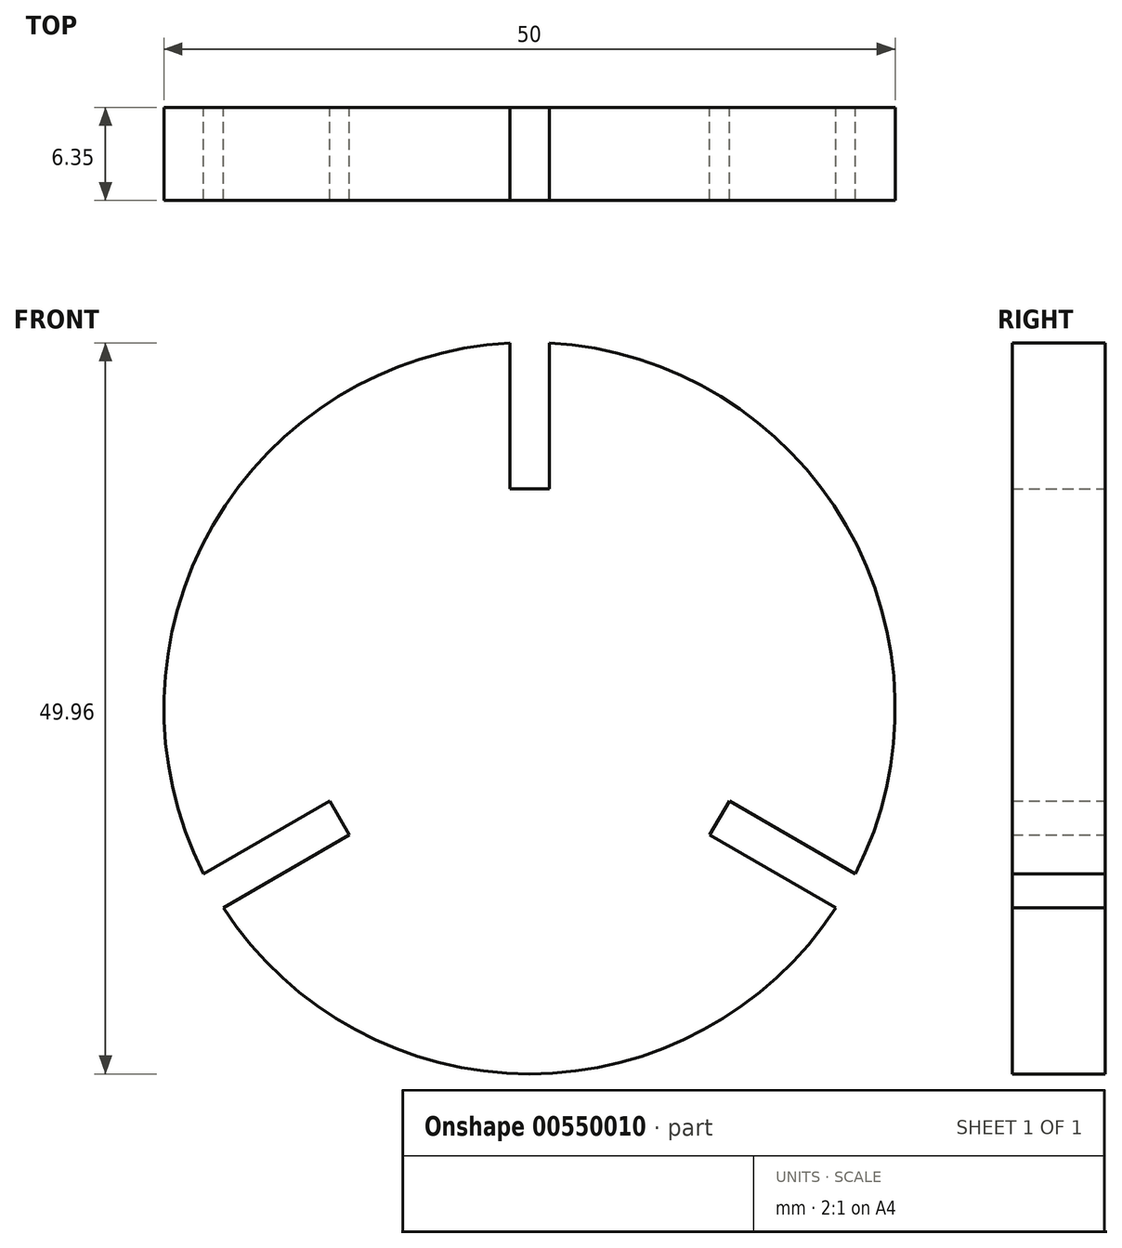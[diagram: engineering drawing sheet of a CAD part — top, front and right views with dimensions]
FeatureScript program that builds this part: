
annotation { "Feature Type Name" : "Feature", "Feature Type Description" : "" }
export const myFeature = defineFeature(function(context is Context, id is Id, definition is map)
    precondition{}
    {
        {
            var Q0;
            Q0=qCreatedBy(makeId("Front.planeOp"),FACE);
            var sketch = newSketch(context, id + "F0", { "sketchPlane" : qUnion([Q0])});
            skArc(sketch, "E0", {"start": v(-1.35, 24.96) * mm, "mid": v(-21.65, 12.5) * mm, "end": v(-22.3, -11.31) * mm});
            skLineSegment(sketch, "E1.bottom", {"start": v(-1.35, 15) * mm, "end": v(1.35, 15) * mm});
            skLineSegment(sketch, "E1.left", {"start": v(-1.35, 15) * mm, "end": v(-1.35, 24.96) * mm});
            skLineSegment(sketch, "E1.right", {"start": v(1.35, 15) * mm, "end": v(1.35, 24.96) * mm});
            skPoint(sketch, "E1.middle", {"position": v(0, 25) * mm});
            skPoint(sketch, "E1.top.end.orphan", {"position": v(1.35, 35) * mm});
            skPoint(sketch, "E1.top.start.orphan", {"position": v(-1.35, 35) * mm});
            skLineSegment(sketch, "E2.1.0", {"start": v(-13.67, -6.33) * mm, "end": v(-22.3, -11.31) * mm});
            skLineSegment(sketch, "E2.1.1", {"start": v(-12.32, -8.67) * mm, "end": v(-20.94, -13.65) * mm});
            skLineSegment(sketch, "E2.1.2", {"start": v(-12.32, -8.67) * mm, "end": v(-13.67, -6.33) * mm});
            skLineSegment(sketch, "E2.2.0", {"start": v(12.32, -8.67) * mm, "end": v(20.94, -13.65) * mm});
            skLineSegment(sketch, "E2.2.1", {"start": v(13.67, -6.33) * mm, "end": v(22.3, -11.31) * mm});
            skLineSegment(sketch, "E2.2.2", {"start": v(13.67, -6.33) * mm, "end": v(12.32, -8.67) * mm});
            skArc(sketch, "E3.trimOffspring", {"start": v(-20.94, -13.65) * mm, "mid": v(0, -25) * mm, "end": v(20.94, -13.65) * mm});
            skArc(sketch, "E4.trimOffspring", {"start": v(22.3, -11.31) * mm, "mid": v(21.65, 12.5) * mm, "end": v(1.35, 24.96) * mm});
            skSolve(sketch);
        }
        {
            var Q0;
            Q0=makeQuery(id+"F0.imprint","IMPRINT",FACE,{"disambiguationData":[TD([[makeQuery(id+"F0.imprint","IMPRINT",EDGE,{"derivedFrom":sQuery(id+"F0.wireOp",EDGE,"E0")}),1.0]])]});
            extrude(context, id + "F1", {"entities" : qUnion([Q0]), "depth" : 6.35 * mm, "offsetDistance" : 25.4 * mm});
        }
    });
